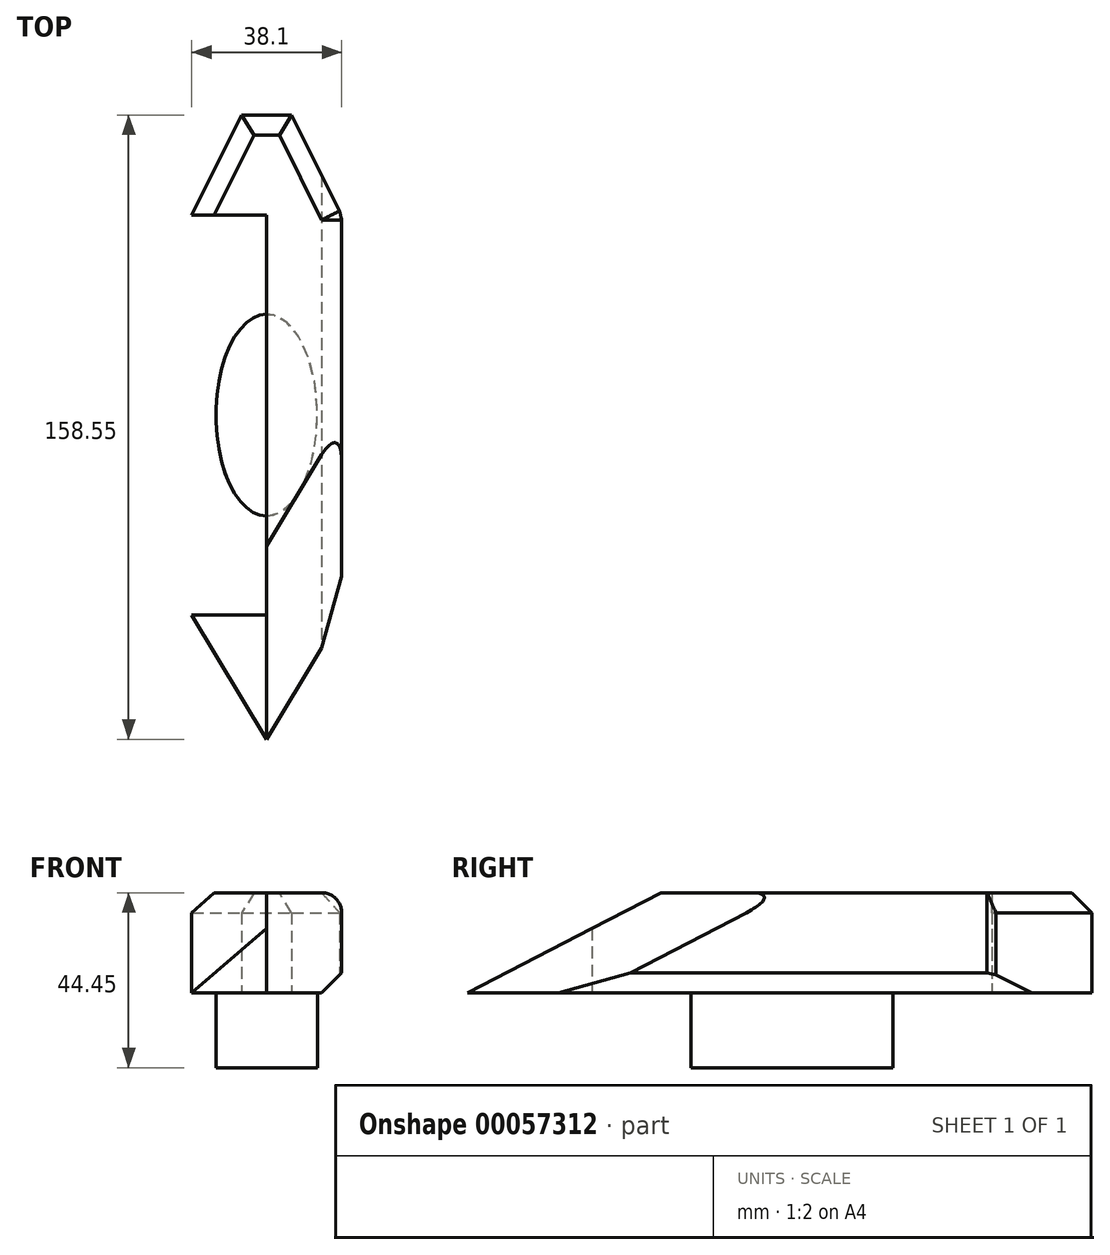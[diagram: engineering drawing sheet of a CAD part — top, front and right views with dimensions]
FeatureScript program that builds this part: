
annotation { "Feature Type Name" : "Feature", "Feature Type Description" : "" }
export const myFeature = defineFeature(function(context is Context, id is Id, definition is map)
    precondition{}
    {
        {
            var Q0;
            Q0=qCreatedBy(makeId("Top.planeOp"),FACE);
            var sketch = newSketch(context, id + "F0", { "sketchPlane" : qUnion([Q0])});
            skLineSegment(sketch, "E0", {"start": v(0, 0) * mm, "end": v(-19.05, 0) * mm});
            skLineSegment(sketch, "E1", {"start": v(19.05, 0) * mm, "end": v(0, 0) * mm});
            skLineSegment(sketch, "E2", {"start": v(0, -31.55) * mm, "end": v(0, 0) * mm});
            skLineSegment(sketch, "E3", {"start": v(-19.05, 0) * mm, "end": v(0, -31.55) * mm});
            skLineSegment(sketch, "E4", {"start": v(0, -31.55) * mm, "end": v(19.05, 0) * mm});
            skLineSegment(sketch, "E5.bottom", {"start": v(-19.05, 0) * mm, "end": v(0, 0) * mm});
            skLineSegment(sketch, "E5.top", {"start": v(-19.05, 101.6) * mm, "end": v(0, 101.6) * mm});
            skLineSegment(sketch, "E5.left", {"start": v(-19.05, 0) * mm, "end": v(-19.05, 101.6) * mm});
            skLineSegment(sketch, "E5.right", {"start": v(0, 0) * mm, "end": v(0, 101.6) * mm});
            skLineSegment(sketch, "E6.top", {"start": v(19.05, 101.6) * mm, "end": v(0, 101.6) * mm});
            skLineSegment(sketch, "E6.left", {"start": v(19.05, 0) * mm, "end": v(19.05, 101.6) * mm});
            skLineSegment(sketch, "E7", {"start": v(0, 101.6) * mm, "end": v(0, 127) * mm});
            skLineSegment(sketch, "E8", {"start": v(0, 127) * mm, "end": v(-6.35, 127) * mm});
            skLineSegment(sketch, "E9", {"start": v(0, 127) * mm, "end": v(6.35, 127) * mm});
            skLineSegment(sketch, "E10", {"start": v(-19.05, 101.6) * mm, "end": v(-6.35, 127) * mm});
            skLineSegment(sketch, "E11", {"start": v(6.35, 127) * mm, "end": v(19.05, 101.6) * mm});
            skSolve(sketch);
        }
        {
            var Q0;
            Q0=makeQuery(id+"F0.imprint","IMPRINT",FACE,{"disambiguationData":[TD([[makeQuery(id+"F0.imprint","IMPRINT",EDGE,{"derivedFrom":sQuery(id+"F0.wireOp",EDGE,"E5.bottom")}),1.0]])]});
            var Q1;
            Q1=makeQuery(id+"F0.imprint","IMPRINT",FACE,{"disambiguationData":[TD([[makeQuery(id+"F0.imprint","IMPRINT",EDGE,{"derivedFrom":sQuery(id+"F0.wireOp",EDGE,"E2")}),-1.0]])]});
            var Q2;
            Q2=makeQuery(id+"F0.imprint","IMPRINT",FACE,{"disambiguationData":[TD([[makeQuery(id+"F0.imprint","IMPRINT",EDGE,{"derivedFrom":sQuery(id+"F0.wireOp",EDGE,"E2")}),1.0]])]});
            var Q3;
            Q3=makeQuery(id+"F0.imprint","IMPRINT",FACE,{"disambiguationData":[TD([[makeQuery(id+"F0.imprint","IMPRINT",EDGE,{"derivedFrom":sQuery(id+"F0.wireOp",EDGE,"E1")}),-1.0]])]});
            var Q4;
            Q4=makeQuery(id+"F0.imprint","IMPRINT",FACE,{"disambiguationData":[TD([[makeQuery(id+"F0.imprint","IMPRINT",EDGE,{"derivedFrom":sQuery(id+"F0.wireOp",EDGE,"E5.top")}),1.0]])]});
            var Q5;
            Q5=makeQuery(id+"F0.imprint","IMPRINT",FACE,{"disambiguationData":[TD([[makeQuery(id+"F0.imprint","IMPRINT",EDGE,{"derivedFrom":sQuery(id+"F0.wireOp",EDGE,"E6.top")}),-1.0]])]});
            extrude(context, id + "F1", {"entities" : qUnion([Q0, Q1, Q2, Q3, Q4, Q5]), "depth" : 25.4 * mm});
        }
        {
            var Q0;
            Q0=qCreatedBy(makeId("Top.planeOp"),FACE);
            var sketch = newSketch(context, id + "F2", { "sketchPlane" : qUnion([Q0])});
            skLineSegment(sketch, "E12", {"start": v(0, 0) * mm, "end": v(0, 50.8) * mm});
            skEllipse(sketch, "E13", {"center": v(0, 50.8) * mm, "majorRadius": 25.65 * mm, "minorRadius": 12.87 * mm, "majorAxis": v(0, -1)});
            skSolve(sketch);
        }
        {
            var Q0;
            Q0=makeQuery(id+"F2.imprint","IMPRINT",FACE,{"disambiguationData":[TD([[makeQuery(id+"F2.imprint","IMPRINT",EDGE,{"derivedFrom":sQuery(id+"F2.wireOp",EDGE,"E13")}),1.0]])]});
            extrude(context, id + "F3", {"entities" : qUnion([Q0]), "operationType" : NewBodyOperationType.ADD, "oppositeDirection" : true, "depth" : 19.05 * mm});
        }
        {
            var Q0;
            Q0=makeQuery(id+"F1.opExtrude","CAP_EDGE",EDGE,{"disambiguationData":[OSD([sQuery(id+"F0.wireOp",EDGE,"E3")])],"isStart":false});
            var Q1;
            Q1=makeQuery(id+"F1.opExtrude","CAP_EDGE",EDGE,{"disambiguationData":[OSD([sQuery(id+"F0.wireOp",EDGE,"E4")])],"isStart":false});
            chamfer(context, id + "F4", {"entities" : qUnion([Q0, Q1]), "width" : 25.4 * mm, "tangentPropagation" : true});
        }
        {
            var Q0;
            Q0=makeQuery(id+"F1.opExtrude","CAP_EDGE",EDGE,{"disambiguationData":[OSD([sQuery(id+"F0.wireOp",EDGE,"E6.left")])],"isStart":false});
            var Q1;
            Q1=makeQuery(id+"F1.opExtrude","CAP_EDGE",EDGE,{"disambiguationData":[OSD([sQuery(id+"F0.wireOp",EDGE,"E5.left")])],"isStart":false});
            fillet(context, id + "F5", {"entities" : qUnion([Q0, Q1]), "radius" : 5.08 * mm, "tangentPropagation" : true, "allowEdgeOverflow" : false});
        }
        {
            var Q0;
            Q0=makeQuery(id+"F1.opExtrude","CAP_EDGE",EDGE,{"disambiguationData":[OSD([sQuery(id+"F0.wireOp",EDGE,"E10")])],"isStart":false});
            var Q1;
            Q1=makeQuery(id+"F1.opExtrude","CAP_EDGE",EDGE,{"disambiguationData":[OSD([sQuery(id+"F0.wireOp",EDGE,"E8"),sQuery(id+"F0.wireOp",EDGE,"E9")])],"isStart":false});
            var Q2;
            Q2=makeQuery(id+"F5.opFillet","BLEND_EDGE",EDGE,{"blendedFrom":[makeQuery(id+"F1.opExtrude","CAP_EDGE",EDGE,{"disambiguationData":[OSD([sQuery(id+"F0.wireOp",EDGE,"E6.left")])],"isStart":false}),makeQuery(id+"F1.opExtrude","SWEPT_FACE",FACE,{"disambiguationData":[OSD([sQuery(id+"F0.wireOp",EDGE,"E11")])]})],"blendedInto":[makeQuery(id+"F1.opExtrude","SWEPT_FACE",FACE,{"disambiguationData":[OSD([sQuery(id+"F0.wireOp",EDGE,"E11")])]})]});
            chamfer(context, id + "F6", {"entities" : qUnion([Q0, Q1, Q2]), "width" : 5.08 * mm, "tangentPropagation" : true});
        }
        {
            var Q0;
            Q0=makeQuery(id+"F1.opExtrude","CAP_EDGE",EDGE,{"disambiguationData":[OSD([sQuery(id+"F0.wireOp",EDGE,"E6.left")])],"isStart":true});
            var Q1;
            Q1=makeQuery(id+"F1.opExtrude","CAP_EDGE",EDGE,{"disambiguationData":[OSD([sQuery(id+"F0.wireOp",EDGE,"E5.left")])],"isStart":true});
            chamfer(context, id + "F7", {"entities" : qUnion([Q0, Q1]), "width" : 5.08 * mm, "tangentPropagation" : true});
        }
    });
